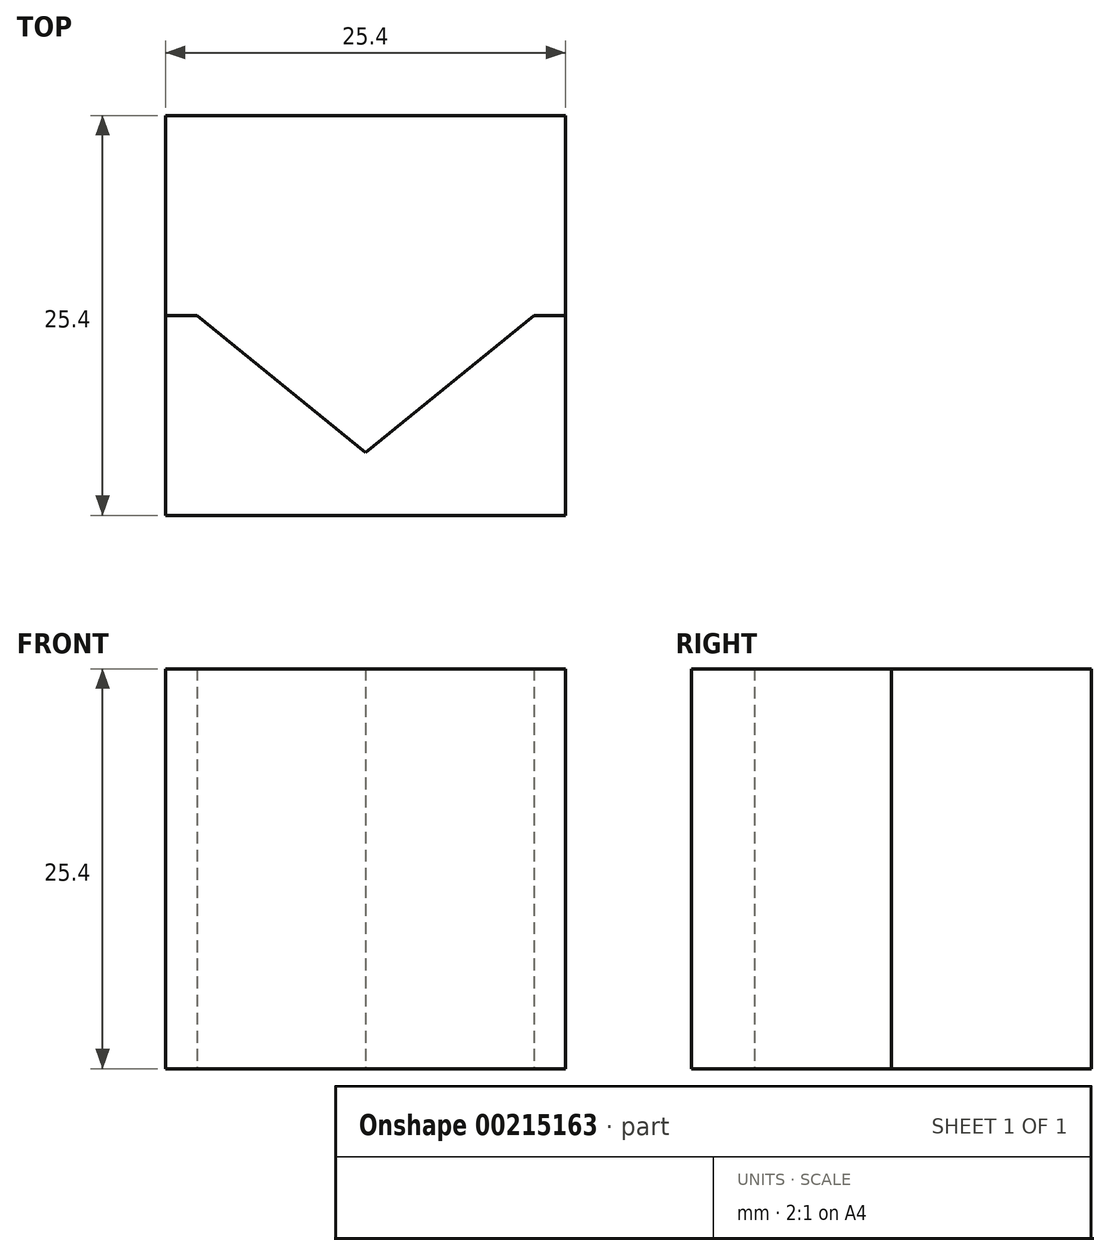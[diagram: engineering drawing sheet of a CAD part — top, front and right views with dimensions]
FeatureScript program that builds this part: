
annotation { "Feature Type Name" : "Feature", "Feature Type Description" : "" }
export const myFeature = defineFeature(function(context is Context, id is Id, definition is map)
    precondition{}
    {
        {
            var Q0;
            Q0=qCreatedBy(makeId("Top.planeOp"),FACE);
            var sketch = newSketch(context, id + "F0", { "sketchPlane" : qUnion([Q0])});
            skLineSegment(sketch, "E0.bottom", {"start": v(0, 0) * mm, "end": v(25.4, 0) * mm});
            skLineSegment(sketch, "E0.top", {"start": v(0, 12.7) * mm, "end": v(25.4, 12.7) * mm});
            skLineSegment(sketch, "E0.left", {"start": v(0, 0) * mm, "end": v(0, 12.7) * mm});
            skLineSegment(sketch, "E0.right", {"start": v(25.4, 0) * mm, "end": v(25.4, 12.7) * mm});
            skSolve(sketch);
        }
        {
            var Q0;
            Q0=makeQuery(id+"F0.imprint","IMPRINT",FACE,{"disambiguationData":[TD([[makeQuery(id+"F0.imprint","IMPRINT",EDGE,{"derivedFrom":sQuery(id+"F0.wireOp",EDGE,"E0.bottom")}),1.0]])]});
            extrude(context, id + "F1", {"entities" : qUnion([Q0]), "depth" : 25.4 * mm});
        }
        {
            var Q0;
            Q0=makeQuery(id+"F1.opExtrude","CAP_FACE",FACE,{"disambiguationData":[OSD([sQuery(id+"F0.wireOp",EDGE,"E0.bottom"),sQuery(id+"F0.wireOp",EDGE,"E0.top"),sQuery(id+"F0.wireOp",EDGE,"E0.left"),sQuery(id+"F0.wireOp",EDGE,"E0.right")])],"isStart":false});
            var sketch = newSketch(context, id + "F2", { "sketchPlane" : qUnion([Q0])});
            skLineSegment(sketch, "E1", {"start": v(2, 12.7) * mm, "end": v(23.4, 12.7) * mm});
            skLineSegment(sketch, "E2", {"start": v(23.4, 12.7) * mm, "end": v(12.7, 4) * mm});
            skLineSegment(sketch, "E3", {"start": v(12.7, 4) * mm, "end": v(2, 12.7) * mm});
            skLineSegment(sketch, "E4", {"start": v(12.7, 12.7) * mm, "end": v(12.7, 0) * mm, "construction": true});
            skSolve(sketch);
        }
        {
            var Q0;
            Q0=makeQuery(id+"F2.imprint","IMPRINT",FACE,{"disambiguationData":[TD([[makeQuery(id+"F2.imprint","IMPRINT",EDGE,{"derivedFrom":sQuery(id+"F2.wireOp",EDGE,"E1")}),-1.0]])]});
            extrude(context, id + "F3", {"entities" : qUnion([Q0]), "operationType" : NewBodyOperationType.REMOVE, "endBound" : BoundingType.THROUGH_ALL, "oppositeDirection" : true, "depth" : 25.4 * mm});
        }
        {
            var Q0;
            Q0=qCreatedBy(makeId("Top.planeOp"),FACE);
            var sketch = newSketch(context, id + "F4", { "sketchPlane" : qUnion([Q0])});
            skLineSegment(sketch, "E5.0", {"start": v(23.4, 12.7) * mm, "end": v(25.4, 12.7) * mm});
            skLineSegment(sketch, "E6.0", {"start": v(23.4, 12.7) * mm, "end": v(12.7, 4) * mm});
            skLineSegment(sketch, "E7.0", {"start": v(12.7, 4) * mm, "end": v(2, 12.7) * mm});
            skLineSegment(sketch, "E8.0", {"start": v(0, 12.7) * mm, "end": v(2, 12.7) * mm});
            skLineSegment(sketch, "E9", {"start": v(25.4, 12.7) * mm, "end": v(25.4, 25.4) * mm});
            skLineSegment(sketch, "E10", {"start": v(25.4, 25.4) * mm, "end": v(0, 25.4) * mm});
            skLineSegment(sketch, "E11", {"start": v(0, 25.4) * mm, "end": v(0, 12.7) * mm});
            skSolve(sketch);
        }
        {
            var Q0;
            Q0=makeQuery(id+"F4.imprint","IMPRINT",FACE,{"disambiguationData":[TD([[makeQuery(id+"F4.imprint","IMPRINT",EDGE,{"derivedFrom":sQuery(id+"F4.wireOp",EDGE,"E5.0")}),1.0]])]});
            extrude(context, id + "F5", {"entities" : qUnion([Q0]), "depth" : 25.4 * mm});
        }
    });
